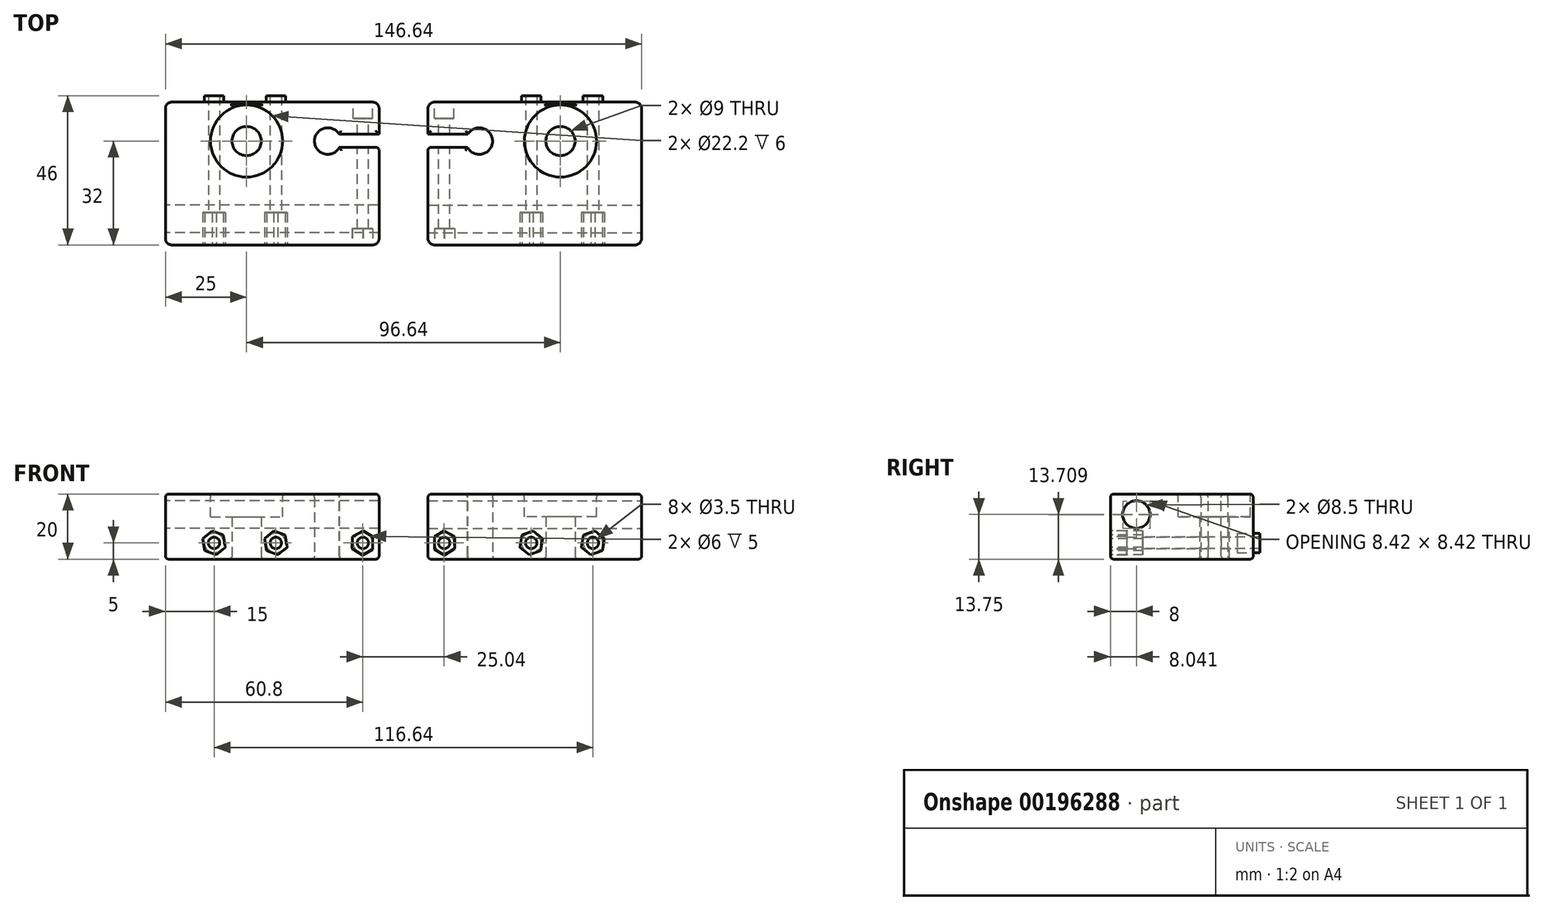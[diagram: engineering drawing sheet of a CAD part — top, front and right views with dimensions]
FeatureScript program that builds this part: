
annotation { "Feature Type Name" : "Feature", "Feature Type Description" : "" }
export const myFeature = defineFeature(function(context is Context, id is Id, definition is map)
    precondition{}
    {
        {
            var Q0;
            Q0=qCreatedBy(makeId("Top.planeOp"),FACE);
            var sketch = newSketch(context, id + "F0", { "sketchPlane" : qUnion([Q0])});
            skLineSegment(sketch, "E0.bottom", {"start": v(-67.48, 12) * mm, "end": v(-1.68, 12) * mm});
            skLineSegment(sketch, "E0.top", {"start": v(-67.48, -32) * mm, "end": v(-1.68, -32) * mm});
            skLineSegment(sketch, "E0.left", {"start": v(-67.48, 12) * mm, "end": v(-67.48, -32) * mm});
            skLineSegment(sketch, "E0.right", {"start": v(-1.68, 12) * mm, "end": v(-1.68, -32) * mm});
            skCircle(sketch, "E1", {"center": v(-51.68, 0) * mm, "radius": 4.1 * mm});
            skPoint(sketch, "E1.centerSnap0", {"position": v(-66.68, 0) * mm});
            skCircle(sketch, "E2", {"center": v(-26.68, 0) * mm, "radius": 4.5 * mm});
            skSolve(sketch);
        }
        {
            var Q0;
            Q0=makeQuery(id+"F0.imprint","IMPRINT",FACE,{"disambiguationData":[TD([[makeQuery(id+"F0.imprint","IMPRINT",EDGE,{"derivedFrom":sQuery(id+"F0.wireOp",EDGE,"E0.bottom")}),-1.0]])]});
            extrude(context, id + "F1", {"entities" : qUnion([Q0]), "depth" : 20 * mm});
        }
        {
            var Q0;
            Q0=makeQuery(id+"F1.opExtrude","SWEPT_FACE",FACE,{"disambiguationData":[OSD([sQuery(id+"F0.wireOp",EDGE,"E0.right")])]});
            var sketch = newSketch(context, id + "F2", { "sketchPlane" : qUnion([Q0])});
            skCircle(sketch, "E3", {"center": v(-24, 13.75) * mm, "radius": 4.25 * mm});
            skPoint(sketch, "E3.centerSnap0", {"position": v(-29.6, 13.75) * mm});
            skSolve(sketch);
        }
        {
            var Q0;
            Q0=makeQuery(id+"F2.imprint","IMPRINT",FACE,{"disambiguationData":[TD([[makeQuery(id+"F2.imprint","IMPRINT",EDGE,{"derivedFrom":sQuery(id+"F2.wireOp",EDGE,"E3")}),1.0]])]});
            var Q1;
            Q1=sQuery(id+"F2.wireOp",EDGE,"E3");
            extrude(context, id + "F3", {"entities" : qUnion([Q0]), "operationType" : NewBodyOperationType.REMOVE, "surfaceEntities" : qUnion([Q1]), "oppositeDirection" : true, "depth" : 70 * mm});
        }
        {
            var Q0;
            Q0=makeQuery(id+"F1.opExtrude","SWEPT_EDGE",EDGE,{"disambiguationData":[OSD([sQuery(id+"F0.wireOp",EDGE,"E0.top"),sQuery(id+"F0.wireOp",EDGE,"E0.left")])]});
            var Q1;
            Q1=makeQuery(id+"F1.opExtrude","SWEPT_EDGE",EDGE,{"disambiguationData":[OSD([sQuery(id+"F0.wireOp",EDGE,"E0.top"),sQuery(id+"F0.wireOp",EDGE,"E0.right")])]});
            var Q2;
            Q2=makeQuery(id+"F1.opExtrude","SWEPT_EDGE",EDGE,{"disambiguationData":[OSD([sQuery(id+"F0.wireOp",EDGE,"E0.bottom"),sQuery(id+"F0.wireOp",EDGE,"E0.right")])]});
            var Q3;
            Q3=makeQuery(id+"F1.opExtrude","SWEPT_EDGE",EDGE,{"disambiguationData":[OSD([sQuery(id+"F0.wireOp",EDGE,"E0.bottom"),sQuery(id+"F0.wireOp",EDGE,"E0.left")])]});
            fillet(context, id + "F4", {"entities" : qUnion([Q0, Q1, Q2, Q3]), "radius" : 2 * mm, "tangentPropagation" : true, "allowEdgeOverflow" : false});
        }
        {
            var Q0;
            Q0=makeQuery(id+"F1.opExtrude","SWEPT_FACE",FACE,{"disambiguationData":[OSD([sQuery(id+"F0.wireOp",EDGE,"E0.bottom")])]});
            var sketch = newSketch(context, id + "F5", { "sketchPlane" : qUnion([Q0])});
            skCircle(sketch, "E4", {"center": v(62.48, 5) * mm, "radius": 1.75 * mm});
            skSolve(sketch);
        }
        {
            var Q0;
            Q0=makeQuery(id+"F5.imprint","IMPRINT",FACE,{"disambiguationData":[TD([[makeQuery(id+"F5.imprint","IMPRINT",EDGE,{"derivedFrom":sQuery(id+"F5.wireOp",EDGE,"E4")}),1.0]])]});
            extrude(context, id + "F6", {"entities" : qUnion([Q0]), "operationType" : NewBodyOperationType.REMOVE, "oppositeDirection" : true, "depth" : 70 * mm});
        }
        {
            var Q0;
            Q0=makeQuery(id+"F1.opExtrude","CAP_FACE",FACE,{"disambiguationData":[OSD([sQuery(id+"F0.wireOp",EDGE,"E0.bottom"),sQuery(id+"F0.wireOp",EDGE,"E0.top"),sQuery(id+"F0.wireOp",EDGE,"E0.left"),sQuery(id+"F0.wireOp",EDGE,"E0.right"),sQuery(id+"F0.wireOp",EDGE,"E1"),sQuery(id+"F0.wireOp",EDGE,"E2")])],"isStart":false});
            var sketch = newSketch(context, id + "F7", { "sketchPlane" : qUnion([Q0])});
            skLineSegment(sketch, "E5.bottom", {"start": v(-54.2, 2.1) * mm, "end": v(-67.48, 2.1) * mm});
            skLineSegment(sketch, "E5.top", {"start": v(-54.2, -1.9) * mm, "end": v(-67.48, -1.9) * mm});
            skLineSegment(sketch, "E5.left", {"start": v(-54.2, 2.1) * mm, "end": v(-54.2, -1.9) * mm});
            skLineSegment(sketch, "E5.right", {"start": v(-67.48, 2.1) * mm, "end": v(-67.48, -1.9) * mm});
            skSolve(sketch);
        }
        {
            var Q0;
            {var subQ0=sQuery(id+"F7.wireOp",EDGE,"E5.right");Q0=makeQuery(id+"F7.imprint","IMPRINT",FACE,{"disambiguationData":[TD([[makeQuery(id+"F7.imprint","IMPRINT",EDGE,{"derivedFrom":subQ0}),1.0]])]});}
            extrude(context, id + "F8", {"entities" : qUnion([Q0]), "operationType" : NewBodyOperationType.REMOVE, "oppositeDirection" : true, "depth" : 30 * mm});
        }
        {
            var Q0;
            {var subQ0=sQuery(id+"F7.wireOp",EDGE,"E5.right");Q0=makeQuery(id+"F7.imprint","IMPRINT",FACE,{"disambiguationData":[TD([[makeQuery(id+"F7.imprint","IMPRINT",EDGE,{"derivedFrom":subQ0}),1.0]])]});}
            extrude(context, id + "F9", {"entities" : qUnion([Q0]), "operationType" : NewBodyOperationType.REMOVE, "oppositeDirection" : true, "depth" : 25 * mm});
        }
        {
            var Q0;
            Q0=makeQuery(id+"F1.opExtrude","SWEPT_FACE",FACE,{"disambiguationData":[OSD([sQuery(id+"F0.wireOp",EDGE,"E0.bottom")])]});
            var sketch = newSketch(context, id + "F10", { "sketchPlane" : qUnion([Q0])});
            skCircle(sketch, "E6", {"center": v(62.48, 5) * mm, "radius": 3 * mm});
            skSolve(sketch);
        }
        {
            var Q0;
            Q0=makeQuery(id+"F10.imprint","IMPRINT",FACE,{"disambiguationData":[TD([[makeQuery(id+"F10.imprint","IMPRINT",EDGE,{"derivedFrom":sQuery(id+"F10.wireOp",EDGE,"E6")}),1.0]])]});
            extrude(context, id + "F11", {"entities" : qUnion([Q0]), "operationType" : NewBodyOperationType.REMOVE, "oppositeDirection" : true, "depth" : 5 * mm});
        }
        {
            var Q0;
            Q0=makeQuery(id+"F1.opExtrude","SWEPT_FACE",FACE,{"disambiguationData":[OSD([sQuery(id+"F0.wireOp",EDGE,"E0.top")])]});
            var sketch = newSketch(context, id + "F12", { "sketchPlane" : qUnion([Q0])});
            skCircle(sketch, "E7.cCircle", {"center": v(-62.48, 5) * mm, "radius": 3.25 * mm, "construction": true});
            skLineSegment(sketch, "E7.0", {"start": v(-62.56, 8.75) * mm, "end": v(-59.27, 6.94) * mm});
            skLineSegment(sketch, "E7.1", {"start": v(-59.27, 6.94) * mm, "end": v(-59.2, 3.2) * mm});
            skLineSegment(sketch, "E7.2", {"start": v(-59.2, 3.2) * mm, "end": v(-62.4, 1.25) * mm});
            skLineSegment(sketch, "E7.3", {"start": v(-62.4, 1.25) * mm, "end": v(-65.7, 3.06) * mm});
            skLineSegment(sketch, "E7.4", {"start": v(-65.7, 3.06) * mm, "end": v(-65.77, 6.8) * mm});
            skLineSegment(sketch, "E7.5", {"start": v(-65.77, 6.8) * mm, "end": v(-62.56, 8.75) * mm});
            skPoint(sketch, "E7.0.midPoint", {"position": v(-60.91, 7.85) * mm});
            skSolve(sketch);
        }
        {
            var Q0;
            Q0=makeQuery(id+"F12.imprint","IMPRINT",FACE,{"disambiguationData":[TD([[makeQuery(id+"F12.imprint","IMPRINT",EDGE,{"derivedFrom":sQuery(id+"F12.wireOp",EDGE,"E7.0")}),-1.0]])]});
            extrude(context, id + "F13", {"entities" : qUnion([Q0]), "operationType" : NewBodyOperationType.REMOVE, "oppositeDirection" : true, "depth" : 5 * mm});
        }
        {
            var Q0;
            Q0=makeQuery(id+"F1.opExtrude","CAP_FACE",FACE,{"disambiguationData":[OSD([sQuery(id+"F0.wireOp",EDGE,"E0.bottom"),sQuery(id+"F0.wireOp",EDGE,"E0.top"),sQuery(id+"F0.wireOp",EDGE,"E0.left"),sQuery(id+"F0.wireOp",EDGE,"E0.right"),sQuery(id+"F0.wireOp",EDGE,"E1"),sQuery(id+"F0.wireOp",EDGE,"E2")])],"isStart":false});
            var sketch = newSketch(context, id + "F14", { "sketchPlane" : qUnion([Q0])});
            skCircle(sketch, "E8", {"center": v(-26.68, 0) * mm, "radius": 11.1 * mm});
            skSolve(sketch);
        }
        {
            var Q0;
            Q0=makeQuery(id+"F14.imprint","IMPRINT",FACE,{"disambiguationData":[TD([[makeQuery(id+"F14.imprint","IMPRINT",EDGE,{"derivedFrom":sQuery(id+"F14.wireOp",EDGE,"E8")}),1.0]])]});
            extrude(context, id + "F15", {"entities" : qUnion([Q0]), "operationType" : NewBodyOperationType.REMOVE, "oppositeDirection" : true, "depth" : 7 * mm});
        }
        {
            var Q0;
            Q0=makeQuery(id+"F1.opExtrude","SWEPT_FACE",FACE,{"disambiguationData":[OSD([sQuery(id+"F0.wireOp",EDGE,"E0.bottom")])]});
            var sketch = newSketch(context, id + "F16", { "sketchPlane" : qUnion([Q0])});
            skCircle(sketch, "E9", {"center": v(16.68, 5) * mm, "radius": 1.75 * mm});
            skCircle(sketch, "E10", {"center": v(35.68, 5) * mm, "radius": 1.75 * mm});
            skCircle(sketch, "E11", {"center": v(35.68, 5) * mm, "radius": 3 * mm});
            skCircle(sketch, "E12", {"center": v(16.68, 5) * mm, "radius": 3 * mm});
            skSolve(sketch);
        }
        {
            var Q0;
            Q0=makeQuery(id+"F16.imprint","IMPRINT",FACE,{"disambiguationData":[TD([[makeQuery(id+"F16.imprint","IMPRINT",EDGE,{"derivedFrom":sQuery(id+"F16.wireOp",EDGE,"E10")}),-1.0]])]});
            var Q1;
            Q1=makeQuery(id+"F16.imprint","IMPRINT",FACE,{"disambiguationData":[TD([[makeQuery(id+"F16.imprint","IMPRINT",EDGE,{"derivedFrom":sQuery(id+"F16.wireOp",EDGE,"E9")}),-1.0]])]});
            extrude(context, id + "F17", {"entities" : qUnion([Q0, Q1]), "operationType" : NewBodyOperationType.ADD, "depth" : 2 * mm});
        }
        {
            var Q0;
            Q0=makeQuery(id+"F16.imprint","IMPRINT",FACE,{"disambiguationData":[TD([[makeQuery(id+"F16.imprint","IMPRINT",EDGE,{"derivedFrom":sQuery(id+"F16.wireOp",EDGE,"E10")}),1.0]])]});
            var Q1;
            Q1=makeQuery(id+"F16.imprint","IMPRINT",FACE,{"disambiguationData":[TD([[makeQuery(id+"F16.imprint","IMPRINT",EDGE,{"derivedFrom":sQuery(id+"F16.wireOp",EDGE,"E9")}),1.0]])]});
            extrude(context, id + "F18", {"entities" : qUnion([Q0, Q1]), "operationType" : NewBodyOperationType.REMOVE, "oppositeDirection" : true, "depth" : 70 * mm});
        }
        {
            var Q0;
            Q0=makeQuery(id+"F1.opExtrude","SWEPT_FACE",FACE,{"disambiguationData":[OSD([sQuery(id+"F0.wireOp",EDGE,"E0.top")])]});
            var sketch = newSketch(context, id + "F19", { "sketchPlane" : qUnion([Q0])});
            skCircle(sketch, "E13.cCircle", {"center": v(-16.68, 5) * mm, "radius": 3.25 * mm, "construction": true});
            skLineSegment(sketch, "E13.0", {"start": v(-19.57, 7.4) * mm, "end": v(-16.05, 8.7) * mm});
            skLineSegment(sketch, "E13.1", {"start": v(-16.05, 8.7) * mm, "end": v(-13.16, 6.3) * mm});
            skLineSegment(sketch, "E13.2", {"start": v(-13.16, 6.3) * mm, "end": v(-13.79, 2.6) * mm});
            skLineSegment(sketch, "E13.3", {"start": v(-13.79, 2.6) * mm, "end": v(-17.3, 1.3) * mm});
            skLineSegment(sketch, "E13.4", {"start": v(-17.3, 1.3) * mm, "end": v(-20.2, 3.7) * mm});
            skLineSegment(sketch, "E13.5", {"start": v(-20.2, 3.7) * mm, "end": v(-19.57, 7.4) * mm});
            skPoint(sketch, "E13.0.midPoint", {"position": v(-17.81, 8.05) * mm});
            skCircle(sketch, "E14.cCircle", {"center": v(-35.68, 5) * mm, "radius": 3.25 * mm, "construction": true});
            skLineSegment(sketch, "E14.0", {"start": v(-38.57, 7.4) * mm, "end": v(-35.05, 8.7) * mm});
            skLineSegment(sketch, "E14.1", {"start": v(-35.05, 8.7) * mm, "end": v(-32.16, 6.3) * mm});
            skLineSegment(sketch, "E14.2", {"start": v(-32.16, 6.3) * mm, "end": v(-32.79, 2.6) * mm});
            skLineSegment(sketch, "E14.3", {"start": v(-32.79, 2.6) * mm, "end": v(-36.3, 1.3) * mm});
            skLineSegment(sketch, "E14.4", {"start": v(-36.3, 1.3) * mm, "end": v(-39.2, 3.7) * mm});
            skLineSegment(sketch, "E14.5", {"start": v(-39.2, 3.7) * mm, "end": v(-38.57, 7.4) * mm});
            skPoint(sketch, "E14.0.midPoint", {"position": v(-36.81, 8.05) * mm});
            skSolve(sketch);
        }
        {
            var Q0;
            Q0=makeQuery(id+"F19.imprint","IMPRINT",FACE,{"disambiguationData":[TD([[makeQuery(id+"F19.imprint","IMPRINT",EDGE,{"derivedFrom":sQuery(id+"F19.wireOp",EDGE,"E13.0")}),-1.0]])]});
            var Q1;
            Q1=makeQuery(id+"F19.imprint","IMPRINT",FACE,{"disambiguationData":[TD([[makeQuery(id+"F19.imprint","IMPRINT",EDGE,{"derivedFrom":sQuery(id+"F19.wireOp",EDGE,"E14.0")}),-1.0]])]});
            extrude(context, id + "F20", {"entities" : qUnion([Q0, Q1]), "operationType" : NewBodyOperationType.REMOVE, "oppositeDirection" : true, "depth" : 10 * mm});
        }
        {
            var Q0;
            Q0=makeQuery(id+"F1.opExtrude","CAP_FACE",FACE,{"disambiguationData":[OSD([sQuery(id+"F0.wireOp",EDGE,"E0.bottom"),sQuery(id+"F0.wireOp",EDGE,"E0.top"),sQuery(id+"F0.wireOp",EDGE,"E0.left"),sQuery(id+"F0.wireOp",EDGE,"E0.right"),sQuery(id+"F0.wireOp",EDGE,"E1"),sQuery(id+"F0.wireOp",EDGE,"E2")])],"isStart":true});
            var Q1;
            Q1=makeQuery(id+"F1.opExtrude","CAP_FACE",FACE,{"disambiguationData":[OSD([sQuery(id+"F0.wireOp",EDGE,"E0.bottom"),sQuery(id+"F0.wireOp",EDGE,"E0.top"),sQuery(id+"F0.wireOp",EDGE,"E0.left"),sQuery(id+"F0.wireOp",EDGE,"E0.right"),sQuery(id+"F0.wireOp",EDGE,"E1"),sQuery(id+"F0.wireOp",EDGE,"E2")])],"isStart":false});
            var Q2;
            Q2=makeQuery(id+"F8.boolean.opBoolean","COPY",EDGE,{"derivedFrom":makeQuery(id+"F8.opExtrude","SWEPT_EDGE",EDGE,{"disambiguationData":[OSD([sQuery(id+"F0.wireOp",EDGE,"E0.left"),sQuery(id+"F7.wireOp",EDGE,"E5.bottom"),sQuery(id+"F7.wireOp",EDGE,"E5.right")])]})});
            var Q3;
            Q3=makeQuery(id+"F8.boolean.opBoolean","COPY",EDGE,{"derivedFrom":makeQuery(id+"F8.opExtrude","SWEPT_EDGE",EDGE,{"disambiguationData":[OSD([sQuery(id+"F0.wireOp",EDGE,"E0.left"),sQuery(id+"F7.wireOp",EDGE,"E5.top"),sQuery(id+"F7.wireOp",EDGE,"E5.right")])]})});
            fillet(context, id + "F21", {"entities" : qUnion([Q0, Q1, Q2, Q3]), "radius" : 1 * mm, "tangentPropagation" : true, "allowEdgeOverflow" : false});
        }
        {
            var Q0;
            Q0=makeQuery(id+"F1.opExtrude","SWEPT_BODY",BODY,{"disambiguationData":[OSD([sQuery(id+"F0.wireOp",EDGE,"E0.bottom"),sQuery(id+"F0.wireOp",EDGE,"E0.top"),sQuery(id+"F0.wireOp",EDGE,"E0.left"),sQuery(id+"F0.wireOp",EDGE,"E0.right"),sQuery(id+"F0.wireOp",EDGE,"E1"),sQuery(id+"F0.wireOp",EDGE,"E2")])]});
            var Q1;
            Q1=qCreatedBy(makeId("Right.planeOp"),FACE);
            mirror(context, id + "F22", {"entities" : qUnion([Q0]), "mirrorPlane" : qUnion([Q1])});
        }
        {
            var Q0;
            Q0=makeQuery(id+"F22.opPattern","COPY",BODY,{"derivedFrom":makeQuery(id+"F1.opExtrude","SWEPT_BODY",BODY,{"disambiguationData":[OSD([sQuery(id+"F0.wireOp",EDGE,"E0.bottom"),sQuery(id+"F0.wireOp",EDGE,"E0.top"),sQuery(id+"F0.wireOp",EDGE,"E0.left"),sQuery(id+"F0.wireOp",EDGE,"E0.right"),sQuery(id+"F0.wireOp",EDGE,"E1"),sQuery(id+"F0.wireOp",EDGE,"E2")])]}),"instanceName":"1"});
            transform(context, id + "F23", {"entities" : qUnion([Q0]), "transformType" : TransformType.TRANSLATION_3D, "dx" : -150 * mm, "dy" : 0 * mm, "dz" : 0 * mm, "makeCopy" : false});
        }
    });
